# Revit family: Plade - VP-V
name_source: partatom
category: Structural Framing
units: mm (PartAtom-declared; Revit-internal decimal feet)

## family parameters
Always export as geometry = No
Always vertical = No
Cut with Voids When Loaded = No
Material for Model Behavior = Other
Section Shape = Not Defined
Shared = No
Show family pre-cut in plan views = Yes
Structural Framing Length Roundoff = 0 mm
Work Plane-Based = Yes

## types (2) — shared parameters
Box Height 1 = 60 mm  [stored 0.19685 ft]
Box Height 2 = 52 mm
CRH_RFA_Bruger_LastRelease = kvnUVH7F
CRH_RFA_Bruger_LastSave = kvnUVH7F
CRH_RFA_TimeStamp_LastRelease = 20250219
CRH_RFA_TimeStamp_LastSave = 20250219
Height = 100 mm  [stored 0.328084 ft]
Length = 2384 mm  [stored 7.82152 ft]
Manufacturer = CRH Concrete
Offset = 15 mm  [stored 0.0492126 ft]
Type Comments = VP
zero-valued in all types: Default Elevation

## per-type parameters (varying)
| type | Type Void | Width |
| VP Vaffel - Hel | Void - Vaffelplade - Hel | 2384 mm  [stored 7.82152 ft] |
| VP Vaffel - Halv | Void - Vaffelplade - Halv | 1194 mm |

note: [stored X ft] marks values corroborated as IEEE doubles in the binary element streams (Revit-internal decimal feet)

## geometry (parser evidence)
native form markers: Sweep x20
no freeform markers — native parametric forms only
